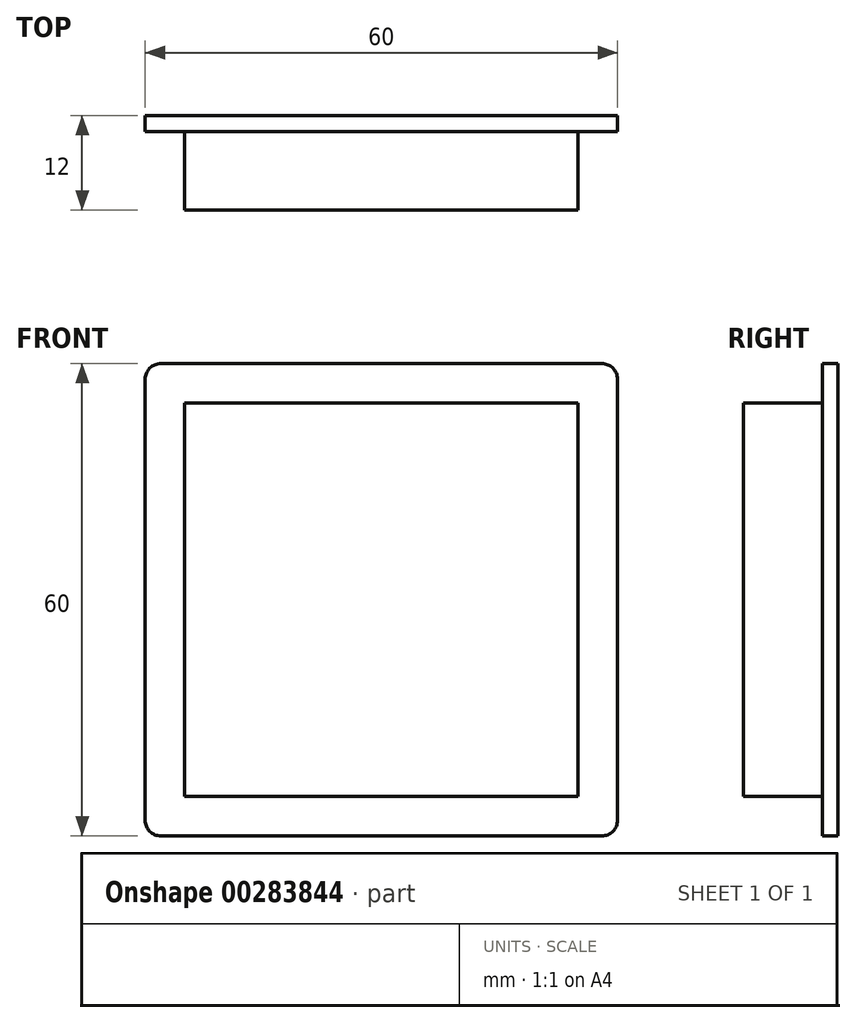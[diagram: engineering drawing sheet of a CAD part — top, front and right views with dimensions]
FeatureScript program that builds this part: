
annotation { "Feature Type Name" : "Feature", "Feature Type Description" : "" }
export const myFeature = defineFeature(function(context is Context, id is Id, definition is map)
    precondition{}
    {
        {
            var Q0;
            Q0=qCreatedBy(makeId("Front.planeOp"),FACE);
            var sketch = newSketch(context, id + "F0", { "sketchPlane" : qUnion([Q0])});
            skLineSegment(sketch, "E0.bottom", {"start": v(-30, -30) * mm, "end": v(30, -30) * mm});
            skLineSegment(sketch, "E0.top", {"start": v(-30, 30) * mm, "end": v(30, 30) * mm});
            skLineSegment(sketch, "E0.left", {"start": v(-30, -30) * mm, "end": v(-30, 30) * mm});
            skLineSegment(sketch, "E0.right", {"start": v(30, -30) * mm, "end": v(30, 30) * mm});
            skPoint(sketch, "E0.middle", {"position": v(0, 0) * mm});
            skSolve(sketch);
        }
        {
            var Q0;
            Q0=makeQuery(id+"F0.imprint","IMPRINT",FACE,{"disambiguationData":[TD([[makeQuery(id+"F0.imprint","IMPRINT",EDGE,{"derivedFrom":sQuery(id+"F0.wireOp",EDGE,"E0.bottom")}),1.0]])]});
            extrude(context, id + "F1", {"entities" : qUnion([Q0]), "depth" : 2 * mm});
        }
        {
            var Q0;
            Q0=makeQuery(id+"F1.opExtrude","CAP_FACE",FACE,{"disambiguationData":[OSD([sQuery(id+"F0.wireOp",EDGE,"E0.bottom"),sQuery(id+"F0.wireOp",EDGE,"E0.top"),sQuery(id+"F0.wireOp",EDGE,"E0.left"),sQuery(id+"F0.wireOp",EDGE,"E0.right")])],"isStart":false});
            var sketch = newSketch(context, id + "F2", { "sketchPlane" : qUnion([Q0])});
            skLineSegment(sketch, "E1.bottom", {"start": v(-25, -25) * mm, "end": v(25, -25) * mm});
            skLineSegment(sketch, "E1.top", {"start": v(-25, 25) * mm, "end": v(25, 25) * mm});
            skLineSegment(sketch, "E1.left", {"start": v(-25, -25) * mm, "end": v(-25, 25) * mm});
            skLineSegment(sketch, "E1.right", {"start": v(25, -25) * mm, "end": v(25, 25) * mm});
            skPoint(sketch, "E1.middle", {"position": v(0, 0) * mm});
            skSolve(sketch);
        }
        {
            var Q0;
            Q0=makeQuery(id+"F2.imprint","IMPRINT",FACE,{"disambiguationData":[TD([[makeQuery(id+"F2.imprint","IMPRINT",EDGE,{"derivedFrom":sQuery(id+"F2.wireOp",EDGE,"E1.bottom")}),1.0]])]});
            extrude(context, id + "F3", {"entities" : qUnion([Q0]), "operationType" : NewBodyOperationType.ADD, "depth" : 10 * mm});
        }
        {
            var Q0;
            Q0=makeQuery(id+"F1.opExtrude","SWEPT_EDGE",EDGE,{"disambiguationData":[OSD([sQuery(id+"F0.wireOp",EDGE,"E0.bottom"),sQuery(id+"F0.wireOp",EDGE,"E0.right")])]});
            var Q1;
            Q1=makeQuery(id+"F1.opExtrude","SWEPT_EDGE",EDGE,{"disambiguationData":[OSD([sQuery(id+"F0.wireOp",EDGE,"E0.top"),sQuery(id+"F0.wireOp",EDGE,"E0.right")])]});
            var Q2;
            Q2=makeQuery(id+"F1.opExtrude","SWEPT_EDGE",EDGE,{"disambiguationData":[OSD([sQuery(id+"F0.wireOp",EDGE,"E0.top"),sQuery(id+"F0.wireOp",EDGE,"E0.left")])]});
            var Q3;
            Q3=makeQuery(id+"F1.opExtrude","SWEPT_EDGE",EDGE,{"disambiguationData":[OSD([sQuery(id+"F0.wireOp",EDGE,"E0.bottom"),sQuery(id+"F0.wireOp",EDGE,"E0.left")])]});
            fillet(context, id + "F4", {"entities" : qUnion([Q0, Q1, Q2, Q3]), "radius" : 2 * mm, "tangentPropagation" : true, "allowEdgeOverflow" : false});
        }
    });
